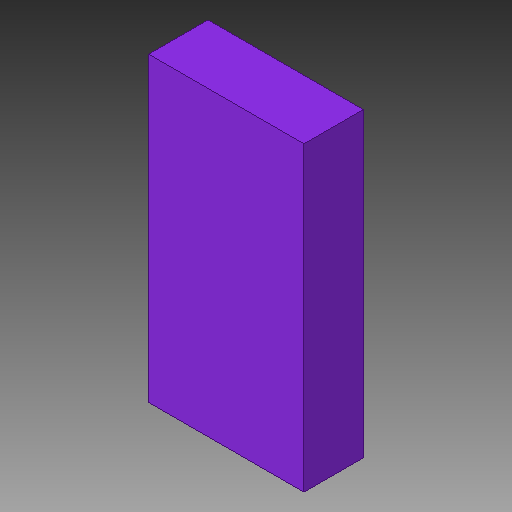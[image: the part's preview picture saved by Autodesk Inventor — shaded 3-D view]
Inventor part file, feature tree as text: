
AUTODESK INVENTOR PART (.ipt)
format: ipt  version: 2018 (Build 220112000, 112)  size: 79,872 bytes
history: native  units: in
note: dims shown in document units (in); Inventor stores cm internally (conversion verified against a paired STEP export)
features: other x1, extrude x1
ambient origin geometry x8: Origin, YZ Plane, XZ Plane, XY Plane, X Axis, Y Axis, Z Axis, Center Point
bodies: Solid1 (feature_tree)
feature tree (2):
  other  "JP1M, SBW_RST_67"
  extrude  "Extrusion1"  Depth=0.0394in TaperAngle=0.0deg
